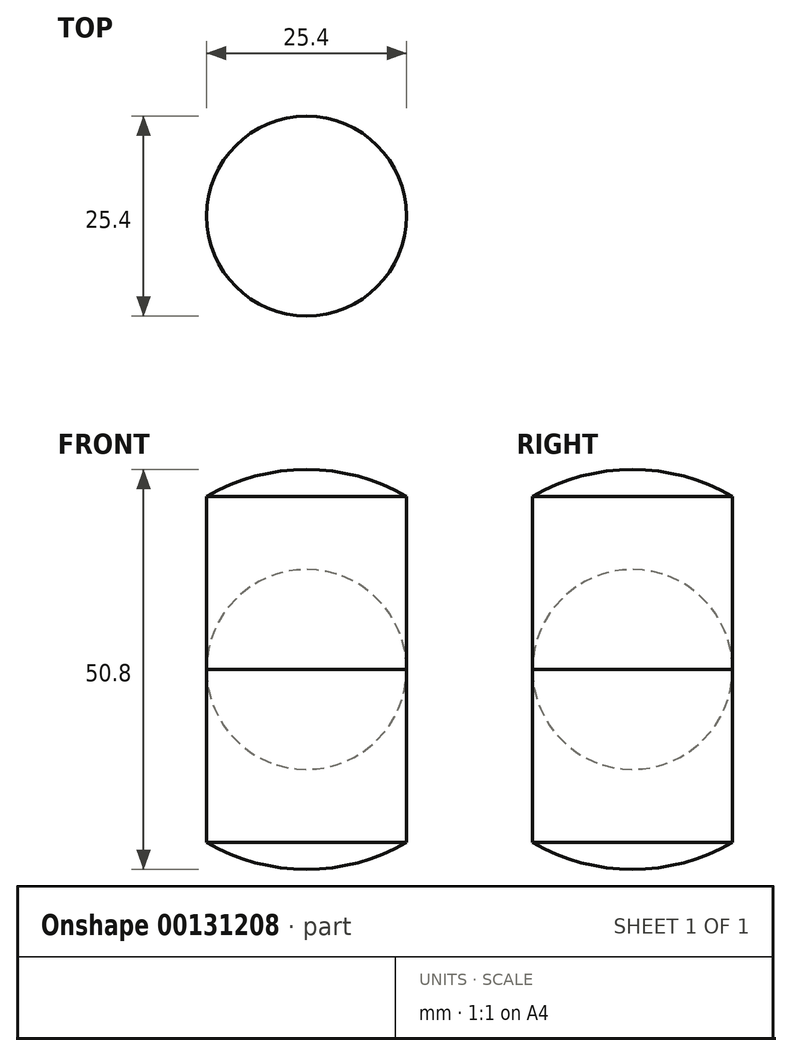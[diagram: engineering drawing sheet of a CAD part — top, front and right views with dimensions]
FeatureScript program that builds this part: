
annotation { "Feature Type Name" : "Feature", "Feature Type Description" : "" }
export const myFeature = defineFeature(function(context is Context, id is Id, definition is map)
    precondition{}
    {
        {
            var Q0;
            Q0=qCreatedBy(makeId("Top.planeOp"),FACE);
            var sketch = newSketch(context, id + "F0", { "sketchPlane" : qUnion([Q0])});
            skCircle(sketch, "E0", {"center": v(0, 0) * mm, "radius": 12.7 * mm});
            skArc(sketch, "E1", {"start": v(0, 25.4) * mm, "mid": v(-25.4, 0) * mm, "end": v(0, -25.4) * mm});
            skLineSegment(sketch, "E2", {"start": v(0, 25.4) * mm, "end": v(0, 12.7) * mm});
            skLineSegment(sketch, "E3.trimOffspring", {"start": v(0, -12.7) * mm, "end": v(0, -25.4) * mm});
            skLineSegment(sketch, "E4", {"start": v(0, 12.7) * mm, "end": v(0, -12.7) * mm});
            skSolve(sketch);
        }
        {
            var Q0;
            Q0=makeQuery(id+"F0.imprint","IMPRINT",FACE,{"disambiguationData":[TD([[makeQuery(id+"F0.imprint","IMPRINT",EDGE,{"derivedFrom":sQuery(id+"F0.wireOp",EDGE,"E1")}),1.0]])]});
            var Q1;
            Q1=sQuery(id+"F0.wireOp",EDGE,"E3.trimOffspring");
            revolve(context, id + "F1", {"entities" : qUnion([Q0]), "axis" : qUnion([Q1]), "revolveType" : RevolveType.FULL});
        }
        {
            var Q0;
            Q0=qCreatedBy(makeId("Top.planeOp"),FACE);
            var sketch = newSketch(context, id + "F2", { "sketchPlane" : qUnion([Q0])});
            skCircle(sketch, "E5", {"center": v(0, 0) * mm, "radius": 12.7 * mm});
            skCircle(sketch, "E6", {"center": v(0, 0) * mm, "radius": 25.4 * mm});
            skSolve(sketch);
        }
        {
            var Q0;
            Q0 = qSketchRegion(id + "F2", true);
            extrude(context, id + "F3", {"entities" : qUnion([Q0]), "operationType" : NewBodyOperationType.REMOVE, "endBound" : BoundingType.SYMMETRIC, "oppositeDirection" : true, "depth" : 50.8 * mm});
        }
    });
